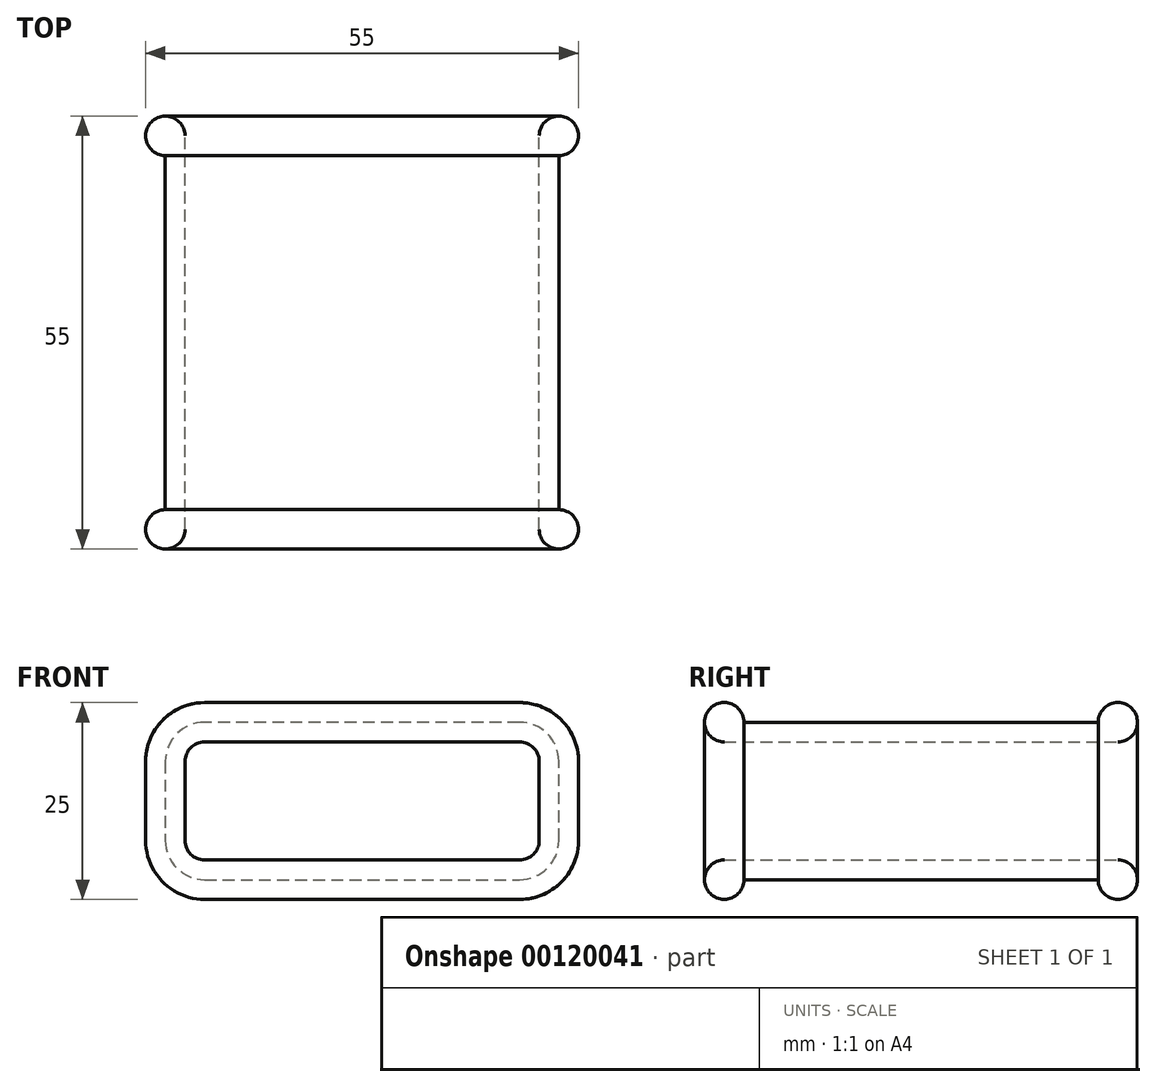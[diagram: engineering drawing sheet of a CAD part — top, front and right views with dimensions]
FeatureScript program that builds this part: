
annotation { "Feature Type Name" : "Feature", "Feature Type Description" : "" }
export const myFeature = defineFeature(function(context is Context, id is Id, definition is map)
    precondition{}
    {
        {
            var Q0;
            Q0=qCreatedBy(makeId("Front.planeOp"),FACE);
            var sketch = newSketch(context, id + "F0", { "sketchPlane" : qUnion([Q0])});
            skLineSegment(sketch, "E0.bottom", {"start": v(20, -10) * mm, "end": v(-20, -10) * mm});
            skLineSegment(sketch, "E0.top", {"start": v(20, 10) * mm, "end": v(0, 10) * mm});
            skLineSegment(sketch, "E0.left", {"start": v(25, -5) * mm, "end": v(25, 5) * mm});
            skLineSegment(sketch, "E0.right", {"start": v(-25, -5) * mm, "end": v(-25, 5) * mm});
            skPoint(sketch, "E0.middle", {"position": v(0, 0) * mm});
            skPoint(sketch, "E1.visualSharp", {"position": v(25, 10) * mm});
            skArc(sketch, "E1.filletArc", {"start": v(25, 5) * mm, "mid": v(23.54, 8.54) * mm, "end": v(20, 10) * mm});
            skPoint(sketch, "E2.visualSharp", {"position": v(25, -10) * mm});
            skArc(sketch, "E2.filletArc", {"start": v(20, -10) * mm, "mid": v(23.54, -8.54) * mm, "end": v(25, -5) * mm});
            skPoint(sketch, "E3.visualSharp", {"position": v(-25, -10) * mm});
            skArc(sketch, "E3.filletArc", {"start": v(-25, -5) * mm, "mid": v(-23.54, -8.54) * mm, "end": v(-20, -10) * mm});
            skPoint(sketch, "E4.visualSharp", {"position": v(-25, 10) * mm});
            skArc(sketch, "E4.filletArc", {"start": v(-20, 10) * mm, "mid": v(-23.54, 8.54) * mm, "end": v(-25, 5) * mm});
            skLineSegment(sketch, "E5", {"start": v(0, 10) * mm, "end": v(-20, 10) * mm});
            skLineSegment(sketch, "E6.bottom", {"start": v(20, -7.5) * mm, "end": v(-20, -7.5) * mm});
            skLineSegment(sketch, "E6.top", {"start": v(20, 7.5) * mm, "end": v(-20, 7.5) * mm});
            skLineSegment(sketch, "E6.left", {"start": v(22.5, -5) * mm, "end": v(22.5, 5) * mm});
            skLineSegment(sketch, "E6.right", {"start": v(-22.5, -5) * mm, "end": v(-22.5, 5) * mm});
            skPoint(sketch, "E7.visualSharp", {"position": v(22.5, 7.5) * mm});
            skArc(sketch, "E7.filletArc", {"start": v(22.5, 5) * mm, "mid": v(21.77, 6.77) * mm, "end": v(20, 7.5) * mm});
            skPoint(sketch, "E8.visualSharp", {"position": v(22.5, -7.5) * mm});
            skArc(sketch, "E8.filletArc", {"start": v(20, -7.5) * mm, "mid": v(21.77, -6.77) * mm, "end": v(22.5, -5) * mm});
            skPoint(sketch, "E9.visualSharp", {"position": v(-22.5, -7.5) * mm});
            skArc(sketch, "E9.filletArc", {"start": v(-22.5, -5) * mm, "mid": v(-21.77, -6.77) * mm, "end": v(-20, -7.5) * mm});
            skPoint(sketch, "E10.visualSharp", {"position": v(-22.5, 7.5) * mm});
            skArc(sketch, "E10.filletArc", {"start": v(-20, 7.5) * mm, "mid": v(-21.77, 6.77) * mm, "end": v(-22.5, 5) * mm});
            skSolve(sketch);
        }
        {
            var Q0;
            Q0=makeQuery(id+"F0.imprint","IMPRINT",FACE,{"disambiguationData":[TD([[makeQuery(id+"F0.imprint","IMPRINT",EDGE,{"derivedFrom":sQuery(id+"F0.wireOp",EDGE,"E0.bottom")}),-1.0]])]});
            extrude(context, id + "F1", {"entities" : qUnion([Q0]), "endBound" : BoundingType.SYMMETRIC, "depth" : 50 * mm});
        }
        {
            var Q0;
            Q0=qCreatedBy(makeId("Right.planeOp"),FACE);
            cPlane(context, id + "F2", {"entities" : qUnion([Q0]), "cplaneType" : CPlaneType.OFFSET, "offset" : 20 * mm, "width" : 150 * mm, "height" : 150 * mm});
        }
        {
            var Q0;
            Q0=qCreatedBy(id+"F2.planeOp",FACE);
            var sketch = newSketch(context, id + "F3", { "sketchPlane" : qUnion([Q0])});
            skCircle(sketch, "E11", {"center": v(-25, 10) * mm, "radius": 2.5 * mm});
            skCircle(sketch, "E12", {"center": v(25, 10) * mm, "radius": 2.5 * mm});
            skSolve(sketch);
        }
        {
            var Q0;
            Q0 = qSketchRegion(id + "F3", true);
            var Q1;
            Q1=makeQuery(id+"F1.opExtrude","CAP_EDGE",EDGE,{"disambiguationData":[OSD([sQuery(id+"F0.wireOp",EDGE,"E0.top"),sQuery(id+"F0.wireOp",EDGE,"E5")])],"isStart":false});
            var Q2;
            Q2=makeQuery(id+"F1.opExtrude","CAP_EDGE",EDGE,{"disambiguationData":[OSD([sQuery(id+"F0.wireOp",EDGE,"E4.filletArc")])],"isStart":false});
            var Q3;
            Q3=makeQuery(id+"F1.opExtrude","CAP_EDGE",EDGE,{"disambiguationData":[OSD([sQuery(id+"F0.wireOp",EDGE,"E0.right")])],"isStart":false});
            var Q4;
            Q4=makeQuery(id+"F1.opExtrude","CAP_EDGE",EDGE,{"disambiguationData":[OSD([sQuery(id+"F0.wireOp",EDGE,"E3.filletArc")])],"isStart":false});
            var Q5;
            Q5=makeQuery(id+"F1.opExtrude","CAP_EDGE",EDGE,{"disambiguationData":[OSD([sQuery(id+"F0.wireOp",EDGE,"E0.bottom")])],"isStart":false});
            var Q6;
            Q6=makeQuery(id+"F1.opExtrude","CAP_EDGE",EDGE,{"disambiguationData":[OSD([sQuery(id+"F0.wireOp",EDGE,"E2.filletArc")])],"isStart":false});
            var Q7;
            Q7=makeQuery(id+"F1.opExtrude","CAP_EDGE",EDGE,{"disambiguationData":[OSD([sQuery(id+"F0.wireOp",EDGE,"E0.left")])],"isStart":false});
            var Q8;
            Q8=makeQuery(id+"F1.opExtrude","CAP_EDGE",EDGE,{"disambiguationData":[OSD([sQuery(id+"F0.wireOp",EDGE,"E1.filletArc")])],"isStart":false});
            sweep(context, id + "F4", {"operationType" : NewBodyOperationType.ADD, "profiles" : qUnion([Q0]), "path" : qUnion([Q1, Q2, Q3, Q4, Q5, Q6, Q7, Q8])});
        }
    });
